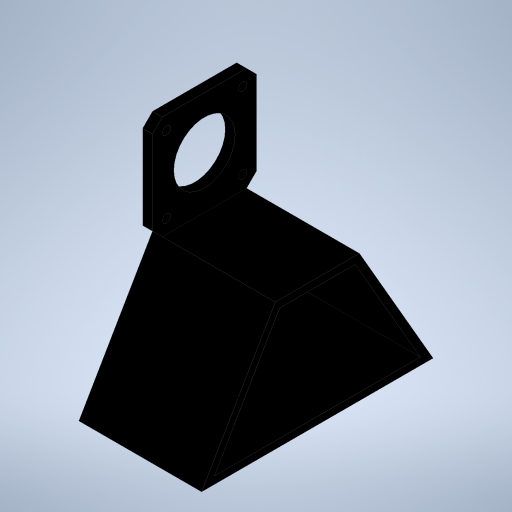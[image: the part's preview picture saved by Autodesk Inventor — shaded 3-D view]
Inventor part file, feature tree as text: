
AUTODESK INVENTOR PART (.ipt)
format: ipt  version: 2023 (Build 270158000, 158)  size: 292,864 bytes
history: native  units: mm
features: sketch x5, extrude x4, chamfer x1, hole x1, shell x1
ambient origin geometry x8: Origin, YZ Plane, XZ Plane, XY Plane, X Axis, Y Axis, Z Axis, Center Point
bodies: Volumenkörper1 (feature_tree)
feature tree (12):
  extrude  "Extrusion1"  Depth=42.3mm
  chamfer  "Fase1"  Distance=4.0mm
  extrude  "Extrusion2"  Depth=4.0mm
  hole  "Bohrung1"  [1 undecoded]
  extrude  "Extrusion3"  Depth=50.0mm
  shell  "Wandung1"  Thickness=15.5mm
  extrude  "Extrusion4"  Depth=50.0mm
  sketch  "Skizze1"  dims[d0=42.3mm d1=42.3mm d2=4.0mm d3=0.0mm]
  sketch  "Skizze2"  dims[d4=4.0mm d5=2.0mm d6=45.0deg d7=25.0mm]
  sketch  "Skizze3"  dims[d8=4.0mm d9=0.0mm]
  sketch  "Skizze4"  dims[d10=3.4mm d11=6.0mm d12=4.0mm d13=2.0mm d14=90.0deg d15=8.0mm d16=20.594885mm d17=15.5mm]
  sketch  "Skizze8"  dims[d18=15.5mm d19=15.5mm d20=15.5mm d21=15.5mm d22=15.5mm d23=15.5mm d24=15.5mm d25=60.0mm d27=60.0mm d28=60.0deg d29=60.0deg d30=50.0mm d31=0.0mm d45=3.0mm d46=50.0mm d47=0.0mm]
note: 1 required parameter value undecoded (feature->parameter linkage not recoverable at this tier; creation-order binding heuristic only, values carry confidence <= 0.55)
